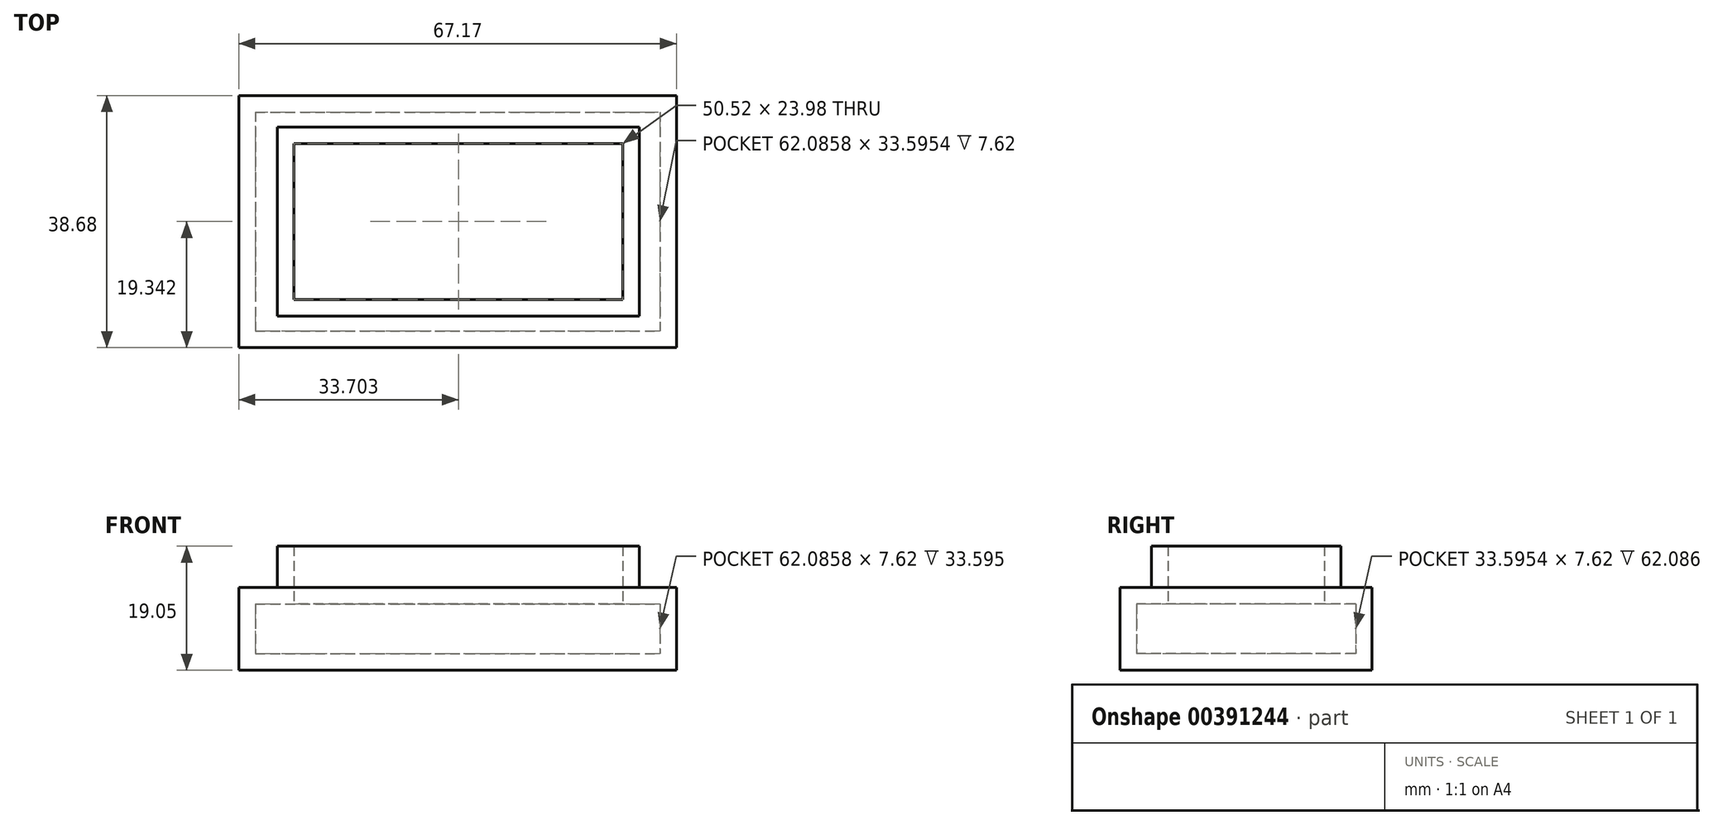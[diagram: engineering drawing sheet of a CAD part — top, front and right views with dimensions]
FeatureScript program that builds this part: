
annotation { "Feature Type Name" : "Feature", "Feature Type Description" : "" }
export const myFeature = defineFeature(function(context is Context, id is Id, definition is map)
    precondition{}
    {
        {
            var Q0;
            Q0=qCreatedBy(makeId("Top.planeOp"),FACE);
            var sketch = newSketch(context, id + "F0", { "sketchPlane" : qUnion([Q0])});
            skLineSegment(sketch, "E0.bottom", {"start": v(0, 0) * mm, "end": v(67.17, 0) * mm});
            skLineSegment(sketch, "E0.top", {"start": v(0, -38.68) * mm, "end": v(67.17, -38.68) * mm});
            skLineSegment(sketch, "E0.left", {"start": v(0, 0) * mm, "end": v(0, -38.68) * mm});
            skLineSegment(sketch, "E0.right", {"start": v(67.17, 0) * mm, "end": v(67.17, -38.68) * mm});
            skSolve(sketch);
        }
        {
            var Q0;
            Q0 = qSketchRegion(id + "F0", true);
            extrude(context, id + "F1", {"entities" : qUnion([Q0]), "depth" : 12.7 * mm});
        }
        {
            var Q0;
            Q0=makeQuery(id+"F1.opExtrude","CAP_FACE",FACE,{"disambiguationData":[OSD([sQuery(id+"F0.wireOp",EDGE,"E0.bottom"),sQuery(id+"F0.wireOp",EDGE,"E0.top"),sQuery(id+"F0.wireOp",EDGE,"E0.left"),sQuery(id+"F0.wireOp",EDGE,"E0.right")])],"isStart":false});
            var sketch = newSketch(context, id + "F2", { "sketchPlane" : qUnion([Q0])});
            skLineSegment(sketch, "E1.bottom", {"start": v(61.5, -4.8) * mm, "end": v(5.9, -4.8) * mm});
            skLineSegment(sketch, "E1.top", {"start": v(61.5, -33.87) * mm, "end": v(5.9, -33.87) * mm});
            skLineSegment(sketch, "E1.left", {"start": v(61.5, -4.8) * mm, "end": v(61.5, -33.87) * mm});
            skLineSegment(sketch, "E1.right", {"start": v(5.9, -4.8) * mm, "end": v(5.9, -33.87) * mm});
            skPoint(sketch, "E1.middle", {"position": v(33.7, -19.34) * mm});
            skPoint(sketch, "E1.middle.positionSnap0", {"position": v(0, -19.34) * mm});
            skPoint(sketch, "E1.centerSnap0", {"position": v(0, -19.34) * mm});
            skSolve(sketch);
        }
        {
            var Q0;
            Q0 = qSketchRegion(id + "F2", true);
            extrude(context, id + "F3", {"entities" : qUnion([Q0]), "operationType" : NewBodyOperationType.ADD, "depth" : 6.35 * mm});
        }
        {
            var Q0;
            Q0=makeQuery(id+"F3.opExtrude","CAP_FACE",FACE,{"disambiguationData":[OSD([sQuery(id+"F2.wireOp",EDGE,"E1.bottom"),sQuery(id+"F2.wireOp",EDGE,"E1.top"),sQuery(id+"F2.wireOp",EDGE,"E1.left"),sQuery(id+"F2.wireOp",EDGE,"E1.right")])],"isStart":false});
            shell(context, id + "F4", {"entities" : qUnion([Q0]), "thickness" : 2.54 * mm});
        }
    });
